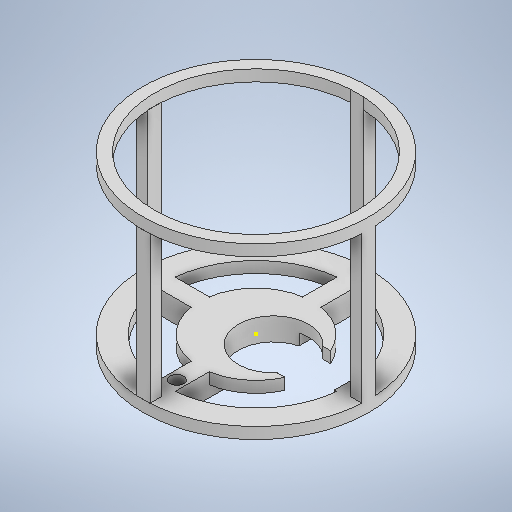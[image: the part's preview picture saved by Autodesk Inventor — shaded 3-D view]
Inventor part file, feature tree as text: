
AUTODESK INVENTOR PART (.ipt)
format: ipt  version: 2025 (Build 290162000, 162)  size: 406,016 bytes
history: native  units: mm
features: sketch x15, extrude x14, other x1
ambient origin geometry x8: Origin, YZ Plane, XZ Plane, XY Plane, X Axis, Y Axis, Z Axis, Center Point
bodies: Body1 (feature_tree)
feature tree (30):
  other  "Bryła1"
  extrude  "Wyciągnięcie proste1"  Depth=100.0mm
  extrude  "Wyciągnięcie proste2"  Depth=80.0mm TaperAngle=0.0deg
  sketch  "Szkic3"
  extrude  "Wyciągnięcie proste3"  Depth=90.0mm
  extrude  "Wyciągnięcie proste4"  Depth=75.0mm TaperAngle=0.0deg
  extrude  "Wyciągnięcie proste5"  Depth=15.0mm
  extrude  "Wyciągnięcie proste6"  Depth=75.0mm TaperAngle=0.0deg
  extrude  "Wyciągnięcie proste7"  Depth=75.0mm TaperAngle=0.0deg
  extrude  "Wyciągnięcie proste8"  Depth=10.0mm TaperAngle=0.0deg
  extrude  "Wyciągnięcie proste9"  Depth=5.0mm TaperAngle=0.0deg
  extrude  "Wyciągnięcie proste10"  Depth=6.0mm
  extrude  "Wyciągnięcie proste11"  Depth=70.0mm TaperAngle=0.0deg
  extrude  "Wyciągnięcie proste12"  Depth=6.0mm
  extrude  "Wyciągnięcie proste13"  Depth=70.0mm TaperAngle=0.0deg
  extrude  "Wyciągnięcie proste17"  Depth=50.0mm
  sketch  "Szkic1"
  sketch  "Szkic2"
  sketch  "Szkic4"
  sketch  "Szkic9"
  sketch  "Szkic10"
  sketch  "Szkic11"
  sketch  "Szkic12"
  sketch  "Szkic13"
  sketch  "Szkic14"
  sketch  "Szkic15"
  sketch  "Szkic16"
  sketch  "Szkic17"
  sketch  "Szkic18"
  sketch  "Szkic22"
